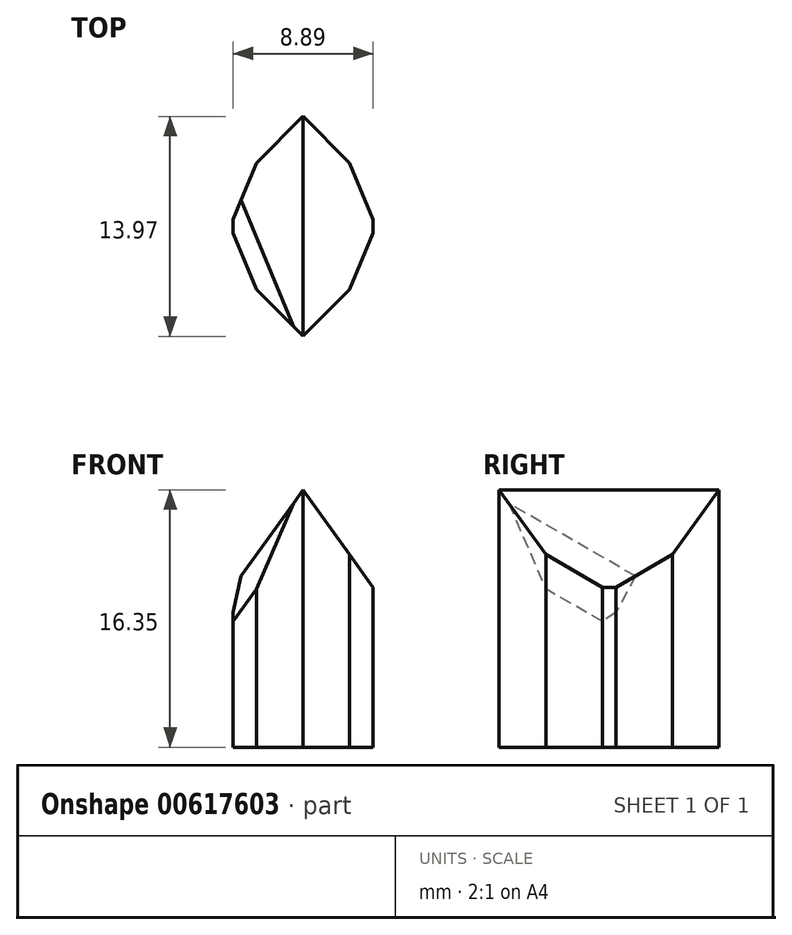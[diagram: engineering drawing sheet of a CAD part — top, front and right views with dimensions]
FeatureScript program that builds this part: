
annotation { "Feature Type Name" : "Feature", "Feature Type Description" : "" }
export const myFeature = defineFeature(function(context is Context, id is Id, definition is map)
    precondition{}
    {
        {
            var Q0;
            Q0=qCreatedBy(makeId("Top.planeOp"),FACE);
            var sketch = newSketch(context, id + "F0", { "sketchPlane" : qUnion([Q0])});
            skLineSegment(sketch, "E0.bottom", {"start": v(-43.84, 21.68) * mm, "end": v(-34.95, 21.68) * mm});
            skLineSegment(sketch, "E0.top", {"start": v(-43.84, 6.44) * mm, "end": v(-34.95, 6.44) * mm});
            skLineSegment(sketch, "E0.left", {"start": v(-43.84, 21.68) * mm, "end": v(-43.84, 6.44) * mm});
            skLineSegment(sketch, "E0.right", {"start": v(-34.95, 21.68) * mm, "end": v(-34.95, 6.44) * mm});
            skSolve(sketch);
        }
        {
            var Q0;
            Q0=makeQuery(id+"F0.imprint","IMPRINT",FACE,{"disambiguationData":[TD([[makeQuery(id+"F0.imprint","IMPRINT",EDGE,{"derivedFrom":sQuery(id+"F0.wireOp",EDGE,"E0.bottom")}),-1.0]])]});
            extrude(context, id + "F1", {"entities" : qUnion([Q0]), "depth" : 10.16 * mm, "offsetDistance" : 25.4 * mm});
        }
        {
            var Q0;
            Q0=makeQuery(id+"F1.opExtrude","SWEPT_FACE",FACE,{"disambiguationData":[OSD([sQuery(id+"F0.wireOp",EDGE,"E0.top")])]});
            var sketch = newSketch(context, id + "F2", { "sketchPlane" : qUnion([Q0])});
            skLineSegment(sketch, "E1", {"start": v(-34.95, 10.16) * mm, "end": v(-43.84, 10.16) * mm});
            skLineSegment(sketch, "E2", {"start": v(-43.84, 10.16) * mm, "end": v(-39.4, 16.35) * mm});
            skLineSegment(sketch, "E3", {"start": v(-34.95, 10.16) * mm, "end": v(-39.4, 16.35) * mm});
            skSolve(sketch);
        }
        {
            var Q0;
            Q0=makeQuery(id+"F2.imprint","IMPRINT",FACE,{"disambiguationData":[TD([[makeQuery(id+"F2.imprint","IMPRINT",EDGE,{"derivedFrom":sQuery(id+"F2.wireOp",EDGE,"E1")}),1.0]])]});
            extrude(context, id + "F3", {"entities" : qUnion([Q0]), "operationType" : NewBodyOperationType.ADD, "oppositeDirection" : true, "depth" : 15.24 * mm, "offsetDistance" : 25.4 * mm});
        }
        {
            var Q0;
            Q0=makeQuery(id+"F1.opExtrude","SWEPT_EDGE",EDGE,{"disambiguationData":[OSD([sQuery(id+"F0.wireOp",EDGE,"E0.top"),sQuery(id+"F0.wireOp",EDGE,"E0.right")])]});
            var Q1;
            Q1=makeQuery(id+"F1.opExtrude","SWEPT_EDGE",EDGE,{"disambiguationData":[OSD([sQuery(id+"F0.wireOp",EDGE,"E0.top"),sQuery(id+"F0.wireOp",EDGE,"E0.left")])]});
            var Q2;
            Q2=makeQuery(id+"F1.opExtrude","SWEPT_EDGE",EDGE,{"disambiguationData":[OSD([sQuery(id+"F0.wireOp",EDGE,"E0.bottom"),sQuery(id+"F0.wireOp",EDGE,"E0.right")])]});
            var Q3;
            Q3=makeQuery(id+"F1.opExtrude","SWEPT_EDGE",EDGE,{"disambiguationData":[OSD([sQuery(id+"F0.wireOp",EDGE,"E0.bottom"),sQuery(id+"F0.wireOp",EDGE,"E0.left")])]});
            chamfer(context, id + "F4", {"entities" : qUnion([Q0, Q1, Q2, Q3]), "width" : 5.08 * mm, "tangentPropagation" : true});
        }
        {
            var Q0;
            {var subQ0=sQuery(id+"F0.wireOp",EDGE,"E0.right");Q0=makeQuery(id+"F4.opChamfer","BLEND_EDGE",EDGE,{"blendedFrom":[makeQuery(id+"F1.opExtrude","SWEPT_EDGE",EDGE,{"disambiguationData":[OSD([sQuery(id+"F0.wireOp",EDGE,"E0.bottom"),subQ0])]}),makeQuery(id+"F1.opExtrude","SWEPT_FACE",FACE,{"disambiguationData":[OSD([subQ0])]})],"blendedInto":[makeQuery(id+"F1.opExtrude","SWEPT_FACE",FACE,{"disambiguationData":[OSD([subQ0])]})]});}
            var Q1;
            {var subQ0=sQuery(id+"F0.wireOp",EDGE,"E0.right");Q1=makeQuery(id+"F4.opChamfer","BLEND_EDGE",EDGE,{"blendedFrom":[makeQuery(id+"F1.opExtrude","SWEPT_EDGE",EDGE,{"disambiguationData":[OSD([sQuery(id+"F0.wireOp",EDGE,"E0.top"),subQ0])]}),makeQuery(id+"F1.opExtrude","SWEPT_FACE",FACE,{"disambiguationData":[OSD([subQ0])]})],"blendedInto":[makeQuery(id+"F1.opExtrude","SWEPT_FACE",FACE,{"disambiguationData":[OSD([subQ0])]})]});}
            var Q2;
            {var subQ0=sQuery(id+"F0.wireOp",EDGE,"E0.left");Q2=makeQuery(id+"F4.opChamfer","BLEND_EDGE",EDGE,{"blendedFrom":[makeQuery(id+"F1.opExtrude","SWEPT_EDGE",EDGE,{"disambiguationData":[OSD([sQuery(id+"F0.wireOp",EDGE,"E0.top"),subQ0])]}),makeQuery(id+"F1.opExtrude","SWEPT_FACE",FACE,{"disambiguationData":[OSD([subQ0])]})],"blendedInto":[makeQuery(id+"F1.opExtrude","SWEPT_FACE",FACE,{"disambiguationData":[OSD([subQ0])]})]});}
            var Q3;
            {var subQ0=sQuery(id+"F0.wireOp",EDGE,"E0.left");Q3=makeQuery(id+"F4.opChamfer","BLEND_EDGE",EDGE,{"blendedFrom":[makeQuery(id+"F1.opExtrude","SWEPT_EDGE",EDGE,{"disambiguationData":[OSD([sQuery(id+"F0.wireOp",EDGE,"E0.bottom"),subQ0])]}),makeQuery(id+"F1.opExtrude","SWEPT_FACE",FACE,{"disambiguationData":[OSD([subQ0])]})],"blendedInto":[makeQuery(id+"F1.opExtrude","SWEPT_FACE",FACE,{"disambiguationData":[OSD([subQ0])]})]});}
            chamfer(context, id + "F5", {"entities" : qUnion([Q0, Q1, Q2, Q3]), "width" : 5.08 * mm, "tangentPropagation" : true});
        }
        {
            var Q0;
            {var subQ0=sQuery(id+"F0.wireOp",EDGE,"E0.left");Q0=makeQuery(id+"F5.opChamfer","BLEND_EDGE",EDGE,{"blendedFrom":[makeQuery(id+"F4.opChamfer","BLEND_EDGE",EDGE,{"blendedFrom":[makeQuery(id+"F1.opExtrude","SWEPT_EDGE",EDGE,{"disambiguationData":[OSD([sQuery(id+"F0.wireOp",EDGE,"E0.top"),subQ0])]}),makeQuery(id+"F1.opExtrude","SWEPT_FACE",FACE,{"disambiguationData":[OSD([subQ0])]})],"blendedInto":[makeQuery(id+"F1.opExtrude","SWEPT_FACE",FACE,{"disambiguationData":[OSD([subQ0])]})]}),makeQuery(id+"F3.opExtrude","SWEPT_FACE",FACE,{"disambiguationData":[OSD([sQuery(id+"F2.wireOp",EDGE,"E2")])]})],"blendedInto":[makeQuery(id+"F3.opExtrude","SWEPT_FACE",FACE,{"disambiguationData":[OSD([sQuery(id+"F2.wireOp",EDGE,"E2")])]})]});}
            chamfer(context, id + "F6", {"entities" : qUnion([Q0]), "width" : 5.08 * mm, "tangentPropagation" : true});
        }
    });
